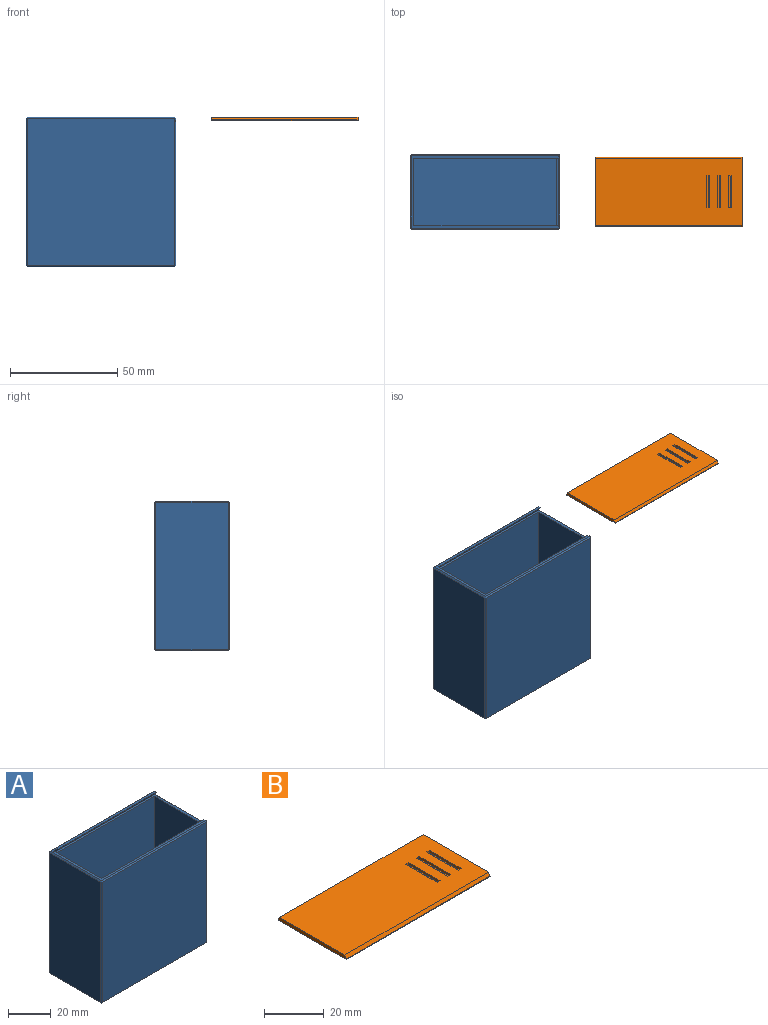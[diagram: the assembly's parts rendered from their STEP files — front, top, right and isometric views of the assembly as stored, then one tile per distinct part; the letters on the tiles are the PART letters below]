
ASSEMBLY  parts=2 mates=1
PART A: 40 faces, bbox 70x35x70 mm
  f0: plane 0.28x0.16mm, normal (1,0,0), area 0mm2, adj f17,f23,f24
  f1: plane 0.28x0.16mm, normal (1,0,0), area 0mm2, adj f18,f25,f26
  f2: plane 67x33.8mm, normal (1,0,0), area 2264.6mm2, adj f16,f20,f23,f26
  f3: plane 66.4x66.4mm, normal (0,1,0), area 4409mm2, adj f8,f11,f12,f13
  f4: plane 66.4x66.4mm, normal (0,-1,0), area 4409mm2, adj f8,f11,f12,f13
  f5: plane 68.8x68.8mm, normal (0,1,0), area 4733.4mm2, adj f22,f23,f33,f34
  f6: plane 68.8x33.8mm, normal (-1,0,0), area 2325.4mm2, adj f28,f33,f36,f39
  f7: plane 68.8x68.8mm, normal (0,-1,0), area 4733.4mm2, adj f26,f27,f35,f36
  f8: plane 68.2x33.48mm, normal (1,0,0), area 2143.4mm2, adj f3,f4,f9,f11,f13,f14,f15
  f9: plane 68.8x33.8mm, normal (0,0,1), area 202.8mm2, adj f8,f14,f15,f24,f25,f34,f35,f39
  f10: plane 68.8x33.8mm, normal (0,0,-1), area 2325.4mm2, adj f16,f22,f27,f28
  f11: plane 66.4x31.4mm, normal (0,0,1), area 2085mm2, adj f3,f4,f8,f12
  f12: plane 66.4x31.4mm, normal (-1,0,0), area 2085mm2, adj f3,f4,f11,f13
  f13: plane 67.6x33.48mm, normal (0,0,1), area 178.2mm2, adj f3,f4,f8,f12,f14,f15,f20
  f14: plane 67.6x1.8mm, normal (0,0.87,-0.5), area 140.5mm2, adj f8,f9,f13,f18
  f15: plane 67.6x1.8mm, normal (0,-0.87,-0.5), area 140.5mm2, adj f8,f9,f13,f17
  f16: plane 33.8x0.6mm, normal (0.71,0,-0.71), area 28.7mm2, adj f2,f10,f19,f21
  f17: plane 2.08x1.52mm, normal (0.71,-0.61,-0.35), area 1.4mm2, adj f0,f15,f20,f23,f24
  f18: plane 2.08x1.52mm, normal (0.71,0.61,-0.35), area 1.4mm2, adj f1,f14,f20,f25,f26
  f19: plane 0.6x0.6mm, normal (0.58,0.58,-0.58), area 0.3mm2, adj f16,f22,f23
  f20: plane 34.44x0.6mm, normal (0.71,0,0.71), area 28.9mm2, adj f2,f13,f17,f18,f23,f26
  f21: plane 0.6x0.6mm, normal (0.58,-0.58,-0.58), area 0.3mm2, adj f16,f26,f27
  f22: plane 68.8x0.6mm, normal (0,0.71,-0.71), area 58.4mm2, adj f5,f10,f19,f29
  f23: plane 68.8x0.6mm, normal (0.71,0.71,0), area 58mm2, adj f0,f2,f5,f17,f19,f20,f30
  f24: plane 1.2x0.6mm, normal (0.71,0,0.71), area 0.6mm2, adj f0,f9,f17,f30
  f25: plane 1.2x0.6mm, normal (0.71,0,0.71), area 0.6mm2, adj f1,f9,f18,f31
  f26: plane 68.8x0.6mm, normal (0.71,-0.71,0), area 58mm2, adj f1,f2,f7,f18,f20,f21,f31
  f27: plane 68.8x0.6mm, normal (0,-0.71,-0.71), area 58.4mm2, adj f7,f10,f21,f32
  f28: plane 33.8x0.6mm, normal (-0.71,0,-0.71), area 28.7mm2, adj f6,f10,f29,f32
  f29: plane 0.6x0.6mm, normal (-0.58,0.58,-0.58), area 0.3mm2, adj f22,f28,f33
  f30: plane 0.6x0.6mm, normal (0.58,0.58,0.58), area 0.3mm2, adj f23,f24,f34
  f31: plane 0.6x0.6mm, normal (0.58,-0.58,0.58), area 0.3mm2, adj f25,f26,f35
  f32: plane 0.6x0.6mm, normal (-0.58,-0.58,-0.58), area 0.3mm2, adj f27,f28,f36
  f33: plane 68.8x0.6mm, normal (-0.71,0.71,0), area 58.4mm2, adj f5,f6,f29,f37
  f34: plane 68.8x0.6mm, normal (0,0.71,0.71), area 58.4mm2, adj f5,f9,f30,f37
  f35: plane 68.8x0.6mm, normal (0,-0.71,0.71), area 58.4mm2, adj f7,f9,f31,f38
  f36: plane 68.8x0.6mm, normal (-0.71,-0.71,0), area 58.4mm2, adj f6,f7,f32,f38
  f37: plane 0.6x0.6mm, normal (-0.58,0.58,0.58), area 0.3mm2, adj f33,f34,f39
  f38: plane 0.6x0.6mm, normal (-0.58,-0.58,0.58), area 0.3mm2, adj f35,f36,f39
  f39: plane 33.8x0.6mm, normal (-0.71,0,0.71), area 28.7mm2, adj f6,f9,f37,f38
PART B: 25 faces, bbox 68.2x32.5x1.8 mm
  f0: plane 68.2x31mm, normal (0,0,1), area 2051.2mm2, adj f2,f3,f4,f5,f6,f7,f8,f10
  f1: plane 67.51x31.88mm, normal (0,0,-1), area 2152mm2, adj f21,f22,f23,f24
  f2: plane 68.2x1.28mm, normal (0,0.87,0.5), area 100.8mm2, adj f0,f4,f5,f23
  f3: plane 68.2x1.28mm, normal (0,-0.87,0.5), area 100.8mm2, adj f0,f4,f5,f22
  f4: plane 32.48x1.45mm, normal (1,0,0), area 46.2mm2, adj f0,f2,f3,f22,f23,f24
  f5: plane 32.48x1.45mm, normal (-1,0,0), area 46.2mm2, adj f0,f2,f3,f21,f22,f23
  f6: plane 1.4x0.9mm, normal (0,-1,0), area 0.9mm2, adj f0,f8,f9,f20
  f7: plane 1.4x0.9mm, normal (0,1,0), area 0.9mm2, adj f0,f8,f9,f20
  f8: plane 15x0.9mm, normal (-1,0,0), area 13.5mm2, adj f0,f6,f7,f9
  f9: plane 15x0.5mm, normal (0,0,1), area 7.5mm2, adj f6,f7,f8,f20
  f10: plane 1.4x0.9mm, normal (0,-1,0), area 0.9mm2, adj f0,f12,f13,f19
  f11: plane 1.4x0.9mm, normal (0,1,0), area 0.9mm2, adj f0,f12,f13,f19
  f12: plane 15x0.9mm, normal (-1,0,0), area 13.5mm2, adj f0,f10,f11,f13
  f13: plane 15x0.5mm, normal (0,0,1), area 7.5mm2, adj f10,f11,f12,f19
  f14: plane 1.4x0.9mm, normal (0,-1,0), area 0.9mm2, adj f0,f16,f17,f18
  f15: plane 1.4x0.9mm, normal (0,1,0), area 0.9mm2, adj f0,f16,f17,f18
  f16: plane 15x0.9mm, normal (-1,0,0), area 13.5mm2, adj f0,f14,f15,f17
  f17: plane 15x0.5mm, normal (0,0,1), area 7.5mm2, adj f14,f15,f16,f18
  f18: plane 15x0.9mm, normal (0.71,0,0.71), area 19.1mm2, adj f0,f14,f15,f17
  f19: plane 15x0.9mm, normal (0.71,0,0.71), area 19.1mm2, adj f0,f10,f11,f13
  f20: plane 15x0.9mm, normal (0.71,0,0.71), area 19.1mm2, adj f0,f6,f7,f9
  f21: plane 32.28x0.35mm, normal (-0.71,0,-0.71), area 15.7mm2, adj f1,f5,f22,f23
  f22: plane 68.2x0.52mm, normal (0,-0.87,-0.5), area 40.8mm2, adj f1,f3,f4,f5,f21,f24
  f23: plane 68.2x0.52mm, normal (0,0.87,-0.5), area 40.8mm2, adj f1,f2,f4,f5,f21,f24
  f24: plane 32.28x0.35mm, normal (0.71,0,-0.71), area 15.7mm2, adj f1,f4,f22,f23
PLACE A t=(-35,-17.5,0)mm
PLACE B t=(-19.97,-17.5,68.2)mm
MATE slider B.f5 <-> A.f8  axis (-1,0,0) through (51.83,0,70)mm
